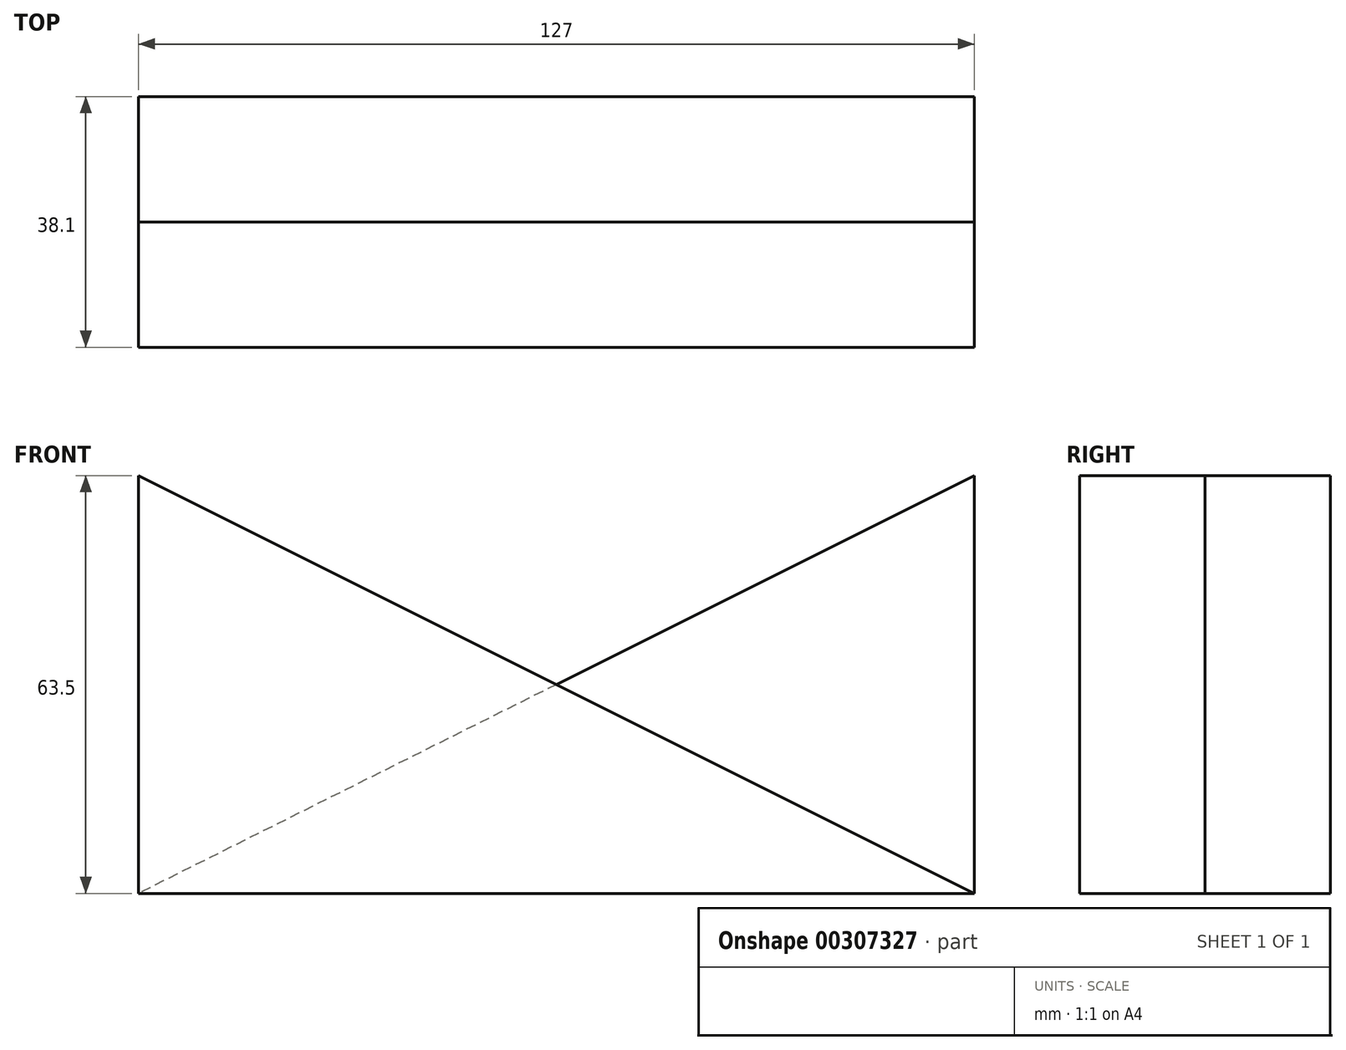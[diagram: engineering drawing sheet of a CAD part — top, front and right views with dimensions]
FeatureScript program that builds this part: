
annotation { "Feature Type Name" : "Feature", "Feature Type Description" : "" }
export const myFeature = defineFeature(function(context is Context, id is Id, definition is map)
    precondition{}
    {
        {
            var Q0;
            Q0=qCreatedBy(makeId("Front.planeOp"),FACE);
            var sketch = newSketch(context, id + "F0", { "sketchPlane" : qUnion([Q0])});
            skLineSegment(sketch, "E0", {"start": v(-51.7, 49.61) * mm, "end": v(-51.7, -13.89) * mm});
            skLineSegment(sketch, "E1", {"start": v(-51.7, -13.89) * mm, "end": v(75.3, -13.89) * mm});
            skLineSegment(sketch, "E2", {"start": v(75.3, -13.89) * mm, "end": v(-51.7, 49.61) * mm});
            skLineSegment(sketch, "E3", {"start": v(75.3, -13.89) * mm, "end": v(75.3, 49.61) * mm});
            skLineSegment(sketch, "E4", {"start": v(75.3, 49.61) * mm, "end": v(-51.7, -13.89) * mm});
            skSolve(sketch);
        }
        {
            var Q0;
            {var subQ0=sQuery(id+"F0.wireOp",EDGE,"E0");Q0=makeQuery(id+"F0.imprint","IMPRINT",FACE,{"disambiguationData":[TD([[makeQuery(id+"F0.imprint","IMPRINT",EDGE,{"derivedFrom":subQ0}),1.0]])]});}
            var Q1;
            {var subQ0=sQuery(id+"F0.wireOp",EDGE,"E1");Q1=makeQuery(id+"F0.imprint","IMPRINT",FACE,{"disambiguationData":[TD([[makeQuery(id+"F0.imprint","IMPRINT",EDGE,{"derivedFrom":subQ0}),1.0]])]});}
            extrude(context, id + "F1", {"entities" : qUnion([Q0, Q1]), "depth" : 19.05 * mm});
        }
        {
            var Q0;
            {var subQ0=sQuery(id+"F0.wireOp",EDGE,"E3");Q0=makeQuery(id+"F0.imprint","IMPRINT",FACE,{"disambiguationData":[TD([[makeQuery(id+"F0.imprint","IMPRINT",EDGE,{"derivedFrom":subQ0}),1.0]])]});}
            var Q1;
            {var subQ0=sQuery(id+"F0.wireOp",EDGE,"E1");Q1=makeQuery(id+"F0.imprint","IMPRINT",FACE,{"disambiguationData":[TD([[makeQuery(id+"F0.imprint","IMPRINT",EDGE,{"derivedFrom":subQ0}),1.0]])]});}
            extrude(context, id + "F2", {"entities" : qUnion([Q0, Q1]), "operationType" : NewBodyOperationType.ADD, "depth" : -19.05 * mm});
        }
    });
